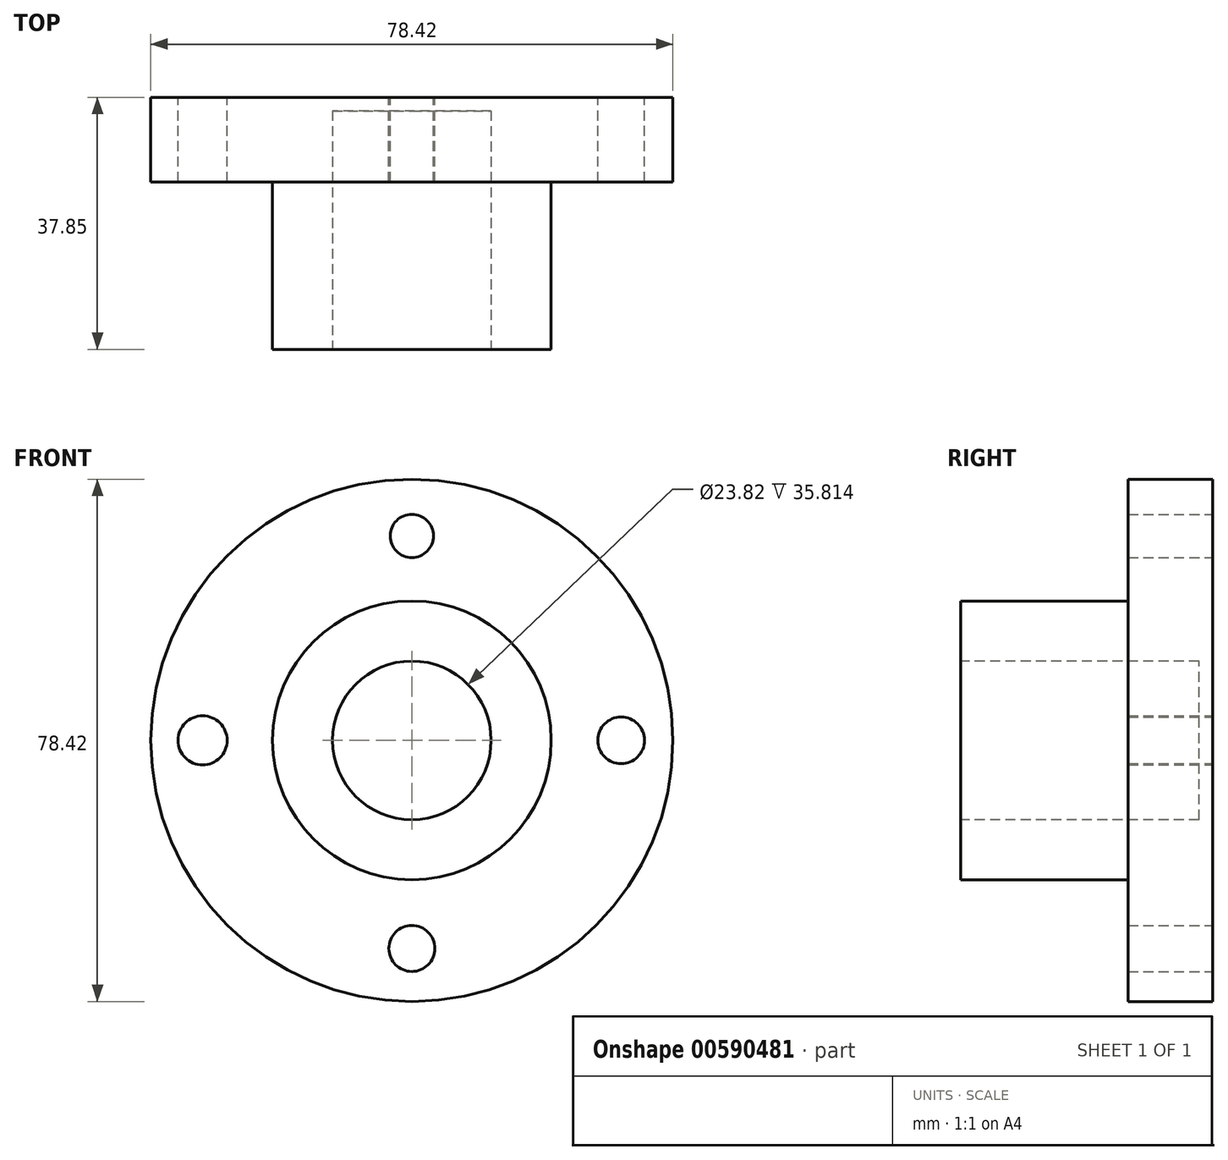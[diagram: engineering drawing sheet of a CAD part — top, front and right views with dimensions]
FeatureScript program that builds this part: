
annotation { "Feature Type Name" : "Feature", "Feature Type Description" : "" }
export const myFeature = defineFeature(function(context is Context, id is Id, definition is map)
    precondition{}
    {
        {
            var Q0;
            Q0=qCreatedBy(makeId("Front.planeOp"),FACE);
            var sketch = newSketch(context, id + "F0", { "sketchPlane" : qUnion([Q0])});
            skCircle(sketch, "E0", {"center": v(0, 0) * mm, "radius": 39.2 * mm});
            skCircle(sketch, "E1", {"center": v(0, 0) * mm, "radius": 20.93 * mm});
            skCircle(sketch, "E2", {"center": v(0, 30.7) * mm, "radius": 3.25 * mm});
            skCircle(sketch, "E3", {"center": v(0, -31.25) * mm, "radius": 3.46 * mm});
            skCircle(sketch, "E4", {"center": v(-31.43, 0) * mm, "radius": 3.68 * mm});
            skCircle(sketch, "E5", {"center": v(31.43, 0) * mm, "radius": 3.5 * mm});
            skSolve(sketch);
        }
        {
            var Q0;
            Q0=makeQuery(id+"F0.imprint","IMPRINT",FACE,{"disambiguationData":[TD([[makeQuery(id+"F0.imprint","IMPRINT",EDGE,{"derivedFrom":sQuery(id+"F0.wireOp",EDGE,"E0")}),1.0]])]});
            extrude(context, id + "F1", {"entities" : qUnion([Q0]), "depth" : 12.7 * mm, "offsetDistance" : 25.4 * mm});
        }
        {
            var Q0;
            Q0=makeQuery(id+"F0.imprint","IMPRINT",FACE,{"disambiguationData":[TD([[makeQuery(id+"F0.imprint","IMPRINT",EDGE,{"derivedFrom":sQuery(id+"F0.wireOp",EDGE,"E1")}),1.0]])]});
            extrude(context, id + "F2", {"entities" : qUnion([Q0]), "operationType" : NewBodyOperationType.ADD, "depth" : 37.85 * mm, "offsetDistance" : 25.4 * mm});
        }
        {
            var Q0;
            Q0=makeQuery(id+"F2.opExtrude","CAP_FACE",FACE,{"disambiguationData":[OSD([sQuery(id+"F0.wireOp",EDGE,"E1")])],"isStart":false});
            var sketch = newSketch(context, id + "F3", { "sketchPlane" : qUnion([Q0])});
            skCircle(sketch, "E6", {"center": v(0, 0) * mm, "radius": 11.9 * mm});
            skSolve(sketch);
        }
        {
            var Q0;
            Q0=makeQuery(id+"F3.imprint","IMPRINT",FACE,{"disambiguationData":[TD([[makeQuery(id+"F3.imprint","IMPRINT",EDGE,{"derivedFrom":sQuery(id+"F3.wireOp",EDGE,"E6")}),1.0]])]});
            extrude(context, id + "F4", {"entities" : qUnion([Q0]), "operationType" : NewBodyOperationType.REMOVE, "oppositeDirection" : true, "depth" : 35.81 * mm, "offsetDistance" : 25.4 * mm});
        }
    });
